# Revit family: Sink-Vanity_Top-Lavatory-KOHLER-Essential-K-30968X-1
name_source: partatom
category: Plumbing Fixtures
units: mm (PartAtom-declared; Revit-internal decimal feet)

## family parameters
Cut with Voids When Loaded = No
Host = Face
OmniClass Number = 23.31.13.00
OmniClass Title = Sinks
Part Type = Normal
Room Calculation Point = No
Round Connector Dimension = Use Diameter
Shared = No

## types (2) — shared parameters
ADA Compliant = No
Assembly Code = D2010400
CW Connection = No
Cold Water Inlet = Cold Water Inlet
Date Modified = 9/26/2024
Default Elevation = 36"
Drain Included = No
Finish = Kohler-Vitreous_China-0-White
HW Connection = No
Height = 7 15/16"
Hot Water Inlet = Hot Water Inlet
Length = 39 3/8"
Manufacturer = Kohler Co.
Master Format 2014 = 22 41 16
Master Format 2014 Name = Residential Lavatories and Sinks
Material = Vitreous China
Product Name = Essential
URL = https://www.kohler.co.th
Vent Connection = No
Waste Connection = Yes
Waste Water Outlet = Waste Water Outlet
WaterSense Certified = No
Width = 20 1/8"

## per-type parameters (varying)
| type | Description | Hole Dist | Hole_1 | Model | Type |
| 1 Hole, 0-White | Integrated Top and Bottom 1000MM 1 Hole | 0" | Yes | K-30968X-1-0 | 1 |
| No Hole, 0-White | Integrated Top and Bottom 1000MM No Hole | 5" | No | K-30968X-0 | 2 |

## geometry (parser evidence)
native form markers: Sweep x5
no freeform markers — native parametric forms only
